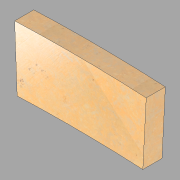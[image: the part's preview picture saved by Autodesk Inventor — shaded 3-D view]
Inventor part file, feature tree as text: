
AUTODESK INVENTOR PART (.ipt)
format: ipt  version: 2022.1 (Build 261234020, 234B)  size: 115,712 bytes
history: imported  units: in
note: dims shown in document units (in); Inventor stores cm internally (conversion verified against a paired STEP export)
features: imported_body x1
ambient origin geometry x8: Origin, YZ Plane, XZ Plane, XY Plane, X Axis, Y Axis, Z Axis, Center Point
bodies: Solid1 (imported_parasolid), Body1 (imported_parasolid)
feature tree (1):
  imported_body  NMx_Import_Brep_tag  [imported B-rep: ~6 faces, bbox_mm=[1047.732119, 514.465119, 152.4]]
